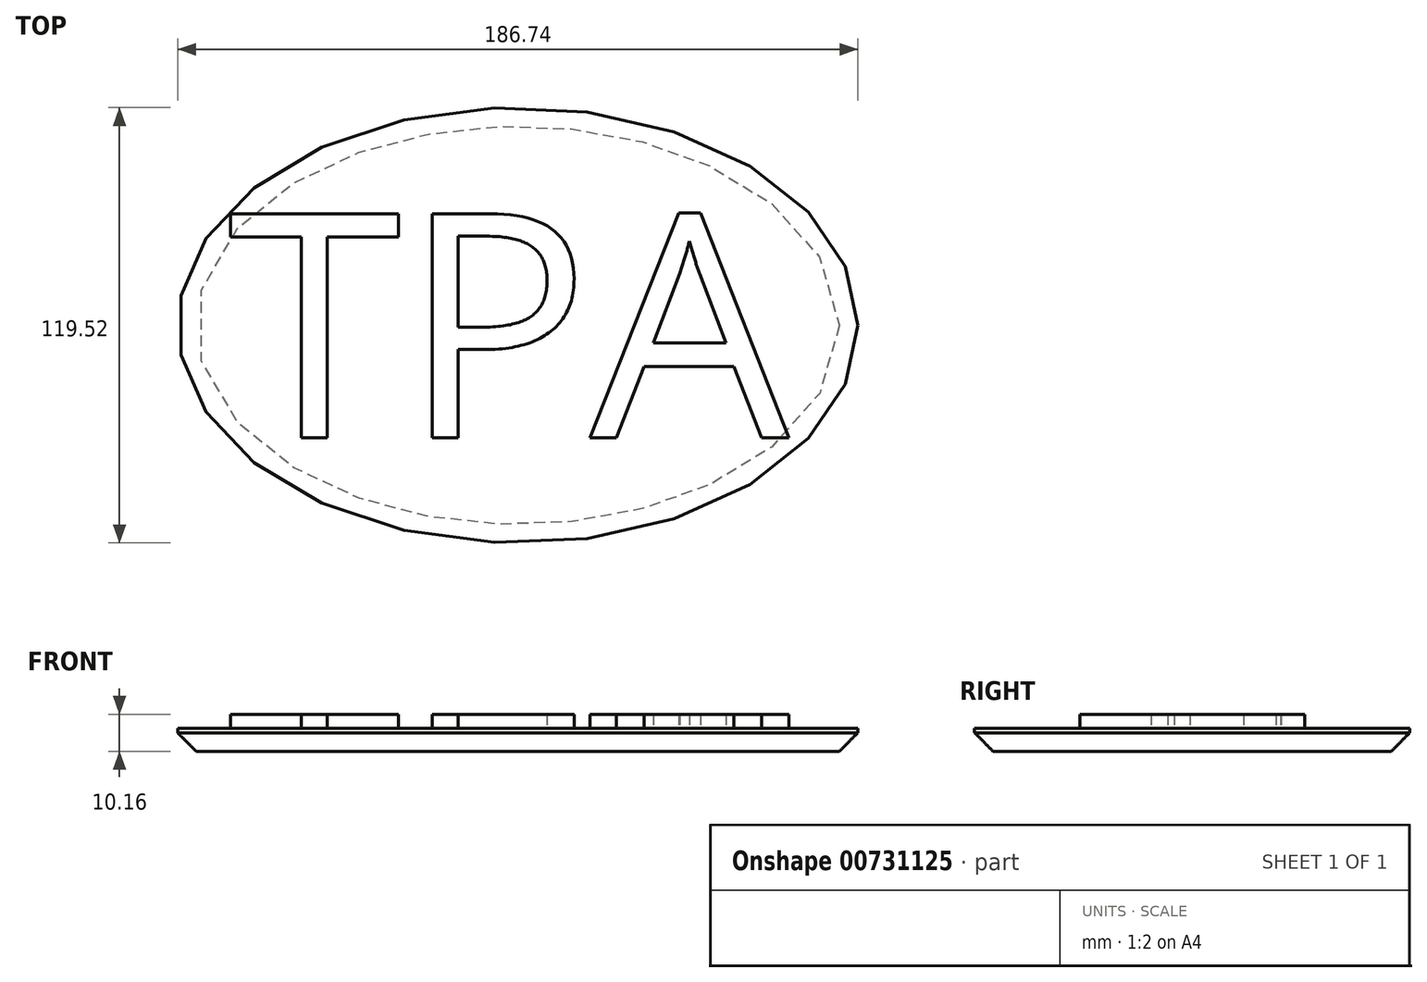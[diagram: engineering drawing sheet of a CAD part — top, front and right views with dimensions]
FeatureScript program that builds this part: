
annotation { "Feature Type Name" : "Feature", "Feature Type Description" : "" }
export const myFeature = defineFeature(function(context is Context, id is Id, definition is map)
    precondition{}
    {
        {
            var Q0;
            Q0=qCreatedBy(makeId("Top.planeOp"),FACE);
            var sketch = newSketch(context, id + "F0", { "sketchPlane" : qUnion([Q0])});
            skEllipse(sketch, "E0", {"center": v(0, 0) * mm, "majorRadius": 93.37 * mm, "minorRadius": 59.76 * mm, "majorAxis": v(1, 0)});
            skSolve(sketch);
        }
        {
            var Q0;
            Q0=makeQuery(id+"F0.imprint","IMPRINT",FACE,{"disambiguationData":[TD([[makeQuery(id+"F0.imprint","IMPRINT",EDGE,{"derivedFrom":sQuery(id+"F0.wireOp",EDGE,"E0")}),1.0]])]});
            extrude(context, id + "F1", {"entities" : qUnion([Q0]), "depth" : 6.35 * mm, "offsetDistance" : 25.4 * mm});
        }
        {
            var Q0;
            Q0=makeQuery(id+"F1.opExtrude","CAP_FACE",FACE,{"disambiguationData":[OSD([sQuery(id+"F0.wireOp",EDGE,"E0")])],"isStart":false});
            var sketch = newSketch(context, id + "F2", { "sketchPlane" : qUnion([Q0])});
            skText(sketch, "E1", { "text": "TPA", "fontName": "OpenSans-Regular.ttf"});
            const initialGuessF2  = {"E1": [-0.07967, -0.03086, 1, 0, 0.06203]};
            skSetInitialGuess(sketch, initialGuessF2);
            skSolve(sketch);
        }
        {
            var Q0;
            Q0 = qSketchRegion(id + "F2", true);
            extrude(context, id + "F3", {"entities" : qUnion([Q0]), "operationType" : NewBodyOperationType.ADD, "depth" : 3.8 * mm, "offsetDistance" : 25.4 * mm});
        }
        {
            var Q0;
            Q0=makeQuery(id+"F1.opExtrude","CAP_EDGE",EDGE,{"disambiguationData":[OSD([sQuery(id+"F0.wireOp",EDGE,"E0")])],"isStart":true});
            chamfer(context, id + "F4", {"entities" : qUnion([Q0]), "width" : 5.08 * mm, "tangentPropagation" : true});
        }
    });
